# Revit family: Wax
name_source: partatom
category: Lighting Fixtures
revit_build: Autodesk Revit Architecture 2014 (Build: 20140709_2115(x64)
units: mm (PartAtom-declared; Revit-internal decimal feet)

## types (1)
- Wax
    Apparent Load = 240 VA
    ArticleNumber = See URL hyperlink
    AssetType = Moveable/Fixed
    BIMObjectName = Wax.rfa
    BSAB 96 = SNB.2
    BallastsCELMAEnergyEfficiencyIndex = Class A1/A2
    CCSClassCode = UAC
    CCSClassName = Belysningsarmatur
    CCSTopnode = L
    Color Filter = 16777215
    Colour = Grey / black
    ControlGearPosition = Integrated
    Description = 70-80-35 General Lighting Systems
    Diameter 1 = 120 mm
    Diameter 2 = 174 mm
    Dimming Lamp Color Temperature Shift = <None>
    DocumentReference = See URL hyperlink
    Documentation = See URL hyperlink
    Finish = Powder coated
    Frame = Riegens_Aluminum_powder coated grey
    HasProtectiveEarth = TRUE
    Height 1 = 265 mm
    IP_Code = IP65
    IfcExportAs = IfcLightFixtureType'
    IfcExportType = NOTDEFINED'
    InsulationStandardClass = Class 2
    InternalFuse = Only required in emergency versions
    LampColourRenderingIndex = Ra>80
    LampType = LED
    LightFixtureMountingType = Pole_side
    LightFixturePlacingType = Pole
    LightSource = LED 3000K / 4000K
    LuminairePowerFactor = >0,9
    LuminaireType = Outdoor Direct LED Luminaire
    Manufacturer = Riegens A/S
    ManufacturerURL = www.riegens.com
    Material = Aluminium and glass
    Model = Wax
    ModelReference = Wax
    NominalVoltage = 220-240V
    Offset from floor = 2865 mm
    Optic = Satin matt reflector, clear front glass and light distributions; Super narrow, narrow, flood and wide flood (tilt head)
    PhaseReference = IEC recommendations
    Photometric Web File = generic
    PhotometricPerformance = In accordance with BS EN 13032-1
    ProductInformation = http://riegens.com
    Shape = Circle
    Size = Ø174 mm
    Tilt Angle = 90.00°
    TotalWattage = Max.
    URL = http://riegens.com
    Uniclass 1.4 = JY73
    Uniclass2 = Pr_70_70_49_43 Light-Emitting Diode (LED) Luminaires
    Version = v.1.0

## geometry (parser evidence)
native form markers: Sweep x4
no freeform markers — native parametric forms only
